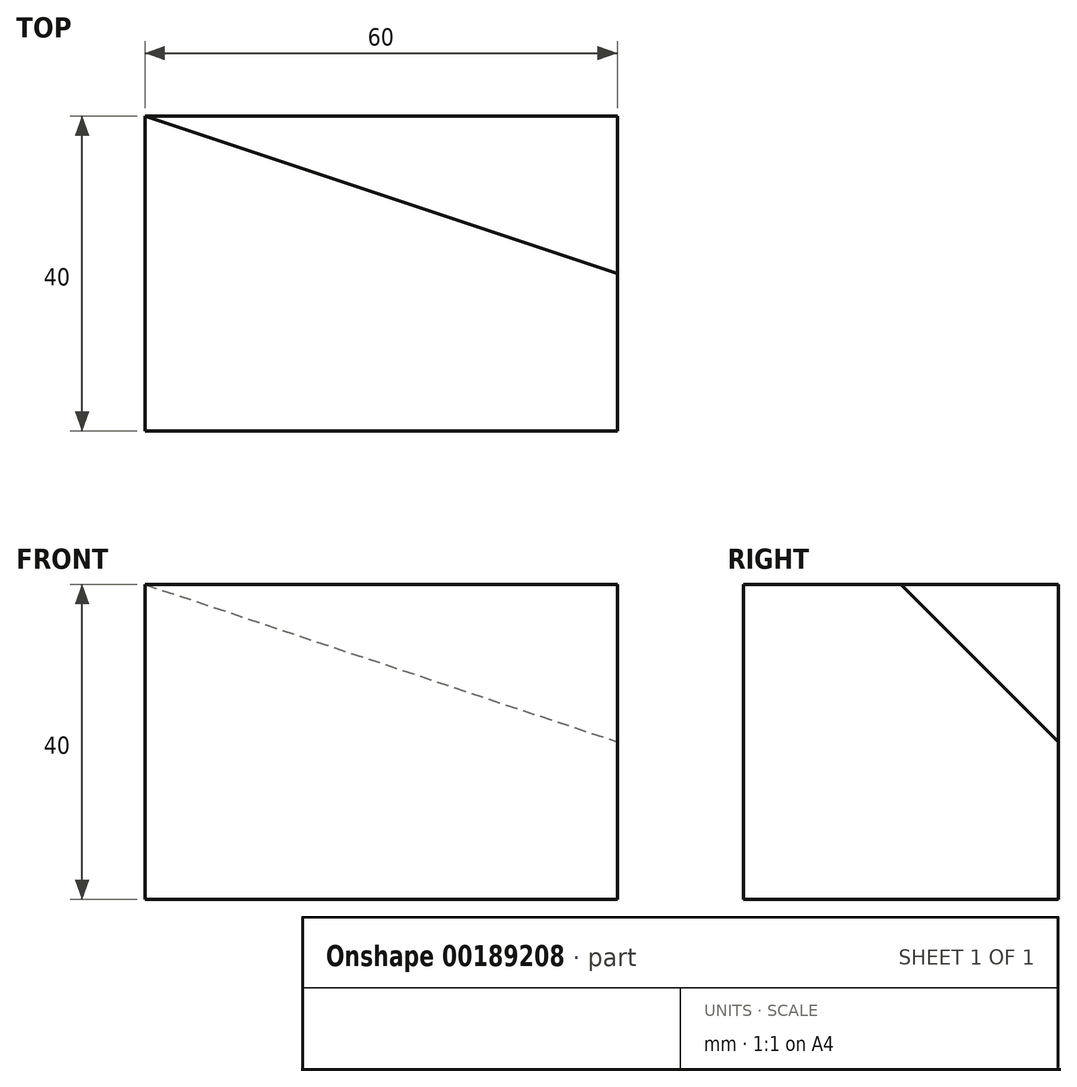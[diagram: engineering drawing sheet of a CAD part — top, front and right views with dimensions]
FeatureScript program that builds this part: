
annotation { "Feature Type Name" : "Feature", "Feature Type Description" : "" }
export const myFeature = defineFeature(function(context is Context, id is Id, definition is map)
    precondition{}
    {
        {
            var Q0;
            Q0=qCreatedBy(makeId("Top.planeOp"),FACE);
            var sketch = newSketch(context, id + "F0", { "sketchPlane" : qUnion([Q0])});
            skLineSegment(sketch, "E0.bottom", {"start": v(0, 0) * mm, "end": v(60, 0) * mm});
            skLineSegment(sketch, "E0.top", {"start": v(0, 40) * mm, "end": v(60, 40) * mm});
            skLineSegment(sketch, "E0.left", {"start": v(0, 0) * mm, "end": v(0, 40) * mm});
            skLineSegment(sketch, "E0.right", {"start": v(60, 0) * mm, "end": v(60, 40) * mm});
            skSolve(sketch);
        }
        {
            var Q0;
            Q0=makeQuery(id+"F0.imprint","IMPRINT",FACE,{"disambiguationData":[TD([[makeQuery(id+"F0.imprint","IMPRINT",EDGE,{"derivedFrom":sQuery(id+"F0.wireOp",EDGE,"E0.bottom")}),1.0]])]});
            extrude(context, id + "F1", {"entities" : qUnion([Q0]), "depth" : 40 * mm});
        }
        {
            var Q0;
            Q0=makeQuery(id+"F1.opExtrude","CAP_EDGE",EDGE,{"disambiguationData":[OSD([sQuery(id+"F0.wireOp",EDGE,"E0.left")])],"isStart":false});
            cPoint(context, id + "F2", {"entities" : qUnion([Q0]), "parameter" : 0.5});
        }
        {
            var Q0;
            Q0=makeQuery(id+"F1.opExtrude","SWEPT_EDGE",EDGE,{"disambiguationData":[OSD([sQuery(id+"F0.wireOp",EDGE,"E0.bottom"),sQuery(id+"F0.wireOp",EDGE,"E0.left")])]});
            cPoint(context, id + "F3", {"entities" : qUnion([Q0]), "parameter" : 0.5});
        }
        {
            var Q0;
            Q0=makeQuery(id+"F1.opExtrude","CAP_VERTEX",VERTEX,{"disambiguationData":[OSD([sQuery(id+"F0.wireOp",EDGE,"E0.bottom"),sQuery(id+"F0.wireOp",EDGE,"E0.right")])],"isStart":false});
            var Q1;
            Q1 = qCreatedBy(id + "F2" ,VERTEX);
            var Q2;
            Q2 = qCreatedBy(id + "F3" ,VERTEX);
            cPlane(context, id + "F4", {"entities" : qUnion([Q0, Q1, Q2]), "cplaneType" : CPlaneType.THREE_POINT, "offset" : 25 * mm, "width" : 150 * mm, "height" : 150 * mm});
        }
        {
            var Q0;
            Q0=qCreatedBy(id+"F4.planeOp",FACE);
            var sketch = newSketch(context, id + "F5", { "sketchPlane" : qUnion([Q0])});
            skLineSegment(sketch, "E1", {"start": v(3.24, -42.43) * mm, "end": v(64.89, -28.28) * mm});
            skLineSegment(sketch, "E2", {"start": v(64.89, -28.28) * mm, "end": v(3.24, -14.14) * mm});
            skLineSegment(sketch, "E3", {"start": v(3.24, -14.14) * mm, "end": v(3.24, -42.43) * mm});
            skSolve(sketch);
        }
        {
            var Q0;
            Q0 = qSketchRegion(id + "F5", true);
            extrude(context, id + "F6", {"entities" : qUnion([Q0]), "operationType" : NewBodyOperationType.REMOVE, "oppositeDirection" : true, "depth" : 25 * mm});
        }
        {
            var Q0;
            Q0=makeQuery(id+"F1.opExtrude","CAP_EDGE",EDGE,{"disambiguationData":[OSD([sQuery(id+"F0.wireOp",EDGE,"E0.right")])],"isStart":false});
            cPoint(context, id + "F7", {"entities" : qUnion([Q0]), "parameter" : 0.5});
        }
        {
            var Q0;
            Q0=makeQuery(id+"F1.opExtrude","SWEPT_EDGE",EDGE,{"disambiguationData":[OSD([sQuery(id+"F0.wireOp",EDGE,"E0.top"),sQuery(id+"F0.wireOp",EDGE,"E0.right")])]});
            cPoint(context, id + "F8", {"entities" : qUnion([Q0]), "parameter" : 0.5});
        }
        {
            var Q0;
            Q0=makeQuery(id+"F1.opExtrude","CAP_VERTEX",VERTEX,{"disambiguationData":[OSD([sQuery(id+"F0.wireOp",EDGE,"E0.top"),sQuery(id+"F0.wireOp",EDGE,"E0.left")])],"isStart":false});
            var Q1;
            Q1 = qCreatedBy(id + "F7" ,VERTEX);
            var Q2;
            Q2 = qCreatedBy(id + "F8" ,VERTEX);
            cPlane(context, id + "F9", {"entities" : qUnion([Q0, Q1, Q2]), "cplaneType" : CPlaneType.THREE_POINT, "offset" : 25 * mm, "width" : 150 * mm, "height" : 150 * mm});
        }
        {
            var Q0;
            Q0=qCreatedBy(id+"F9.planeOp",FACE);
            var sketch = newSketch(context, id + "F10", { "sketchPlane" : qUnion([Q0])});
            skLineSegment(sketch, "E4", {"start": v(-12.98, 0) * mm, "end": v(48.67, -14.14) * mm});
            skLineSegment(sketch, "E5", {"start": v(48.67, -14.14) * mm, "end": v(48.67, 14.14) * mm});
            skLineSegment(sketch, "E6", {"start": v(48.67, 14.14) * mm, "end": v(-12.98, 0) * mm});
            skSolve(sketch);
        }
        {
            var Q0;
            Q0 = qSketchRegion(id + "F10", true);
            extrude(context, id + "F11", {"entities" : qUnion([Q0]), "operationType" : NewBodyOperationType.REMOVE, "oppositeDirection" : true, "depth" : 25 * mm});
        }
    });
